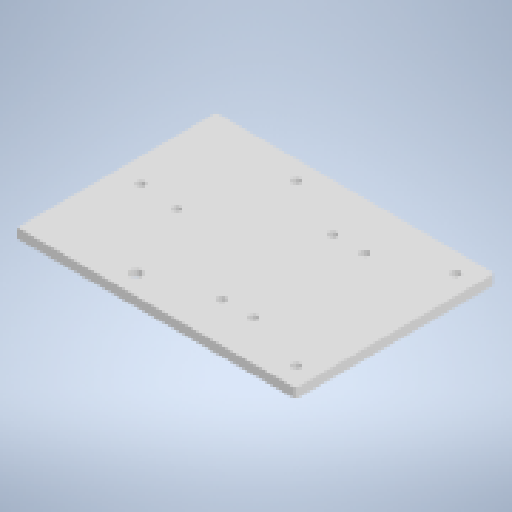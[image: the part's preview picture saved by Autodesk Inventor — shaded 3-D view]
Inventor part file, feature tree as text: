
AUTODESK INVENTOR PART (.ipt)
format: ipt  version: 2023.2 (Build 272271000, 271)  size: 173,056 bytes
history: native  units: mm
features: hole x4, reference x4, other x4, sketch x3, extrude x1, fillet x1
ambient origin geometry x8: Origin, YZ Plane, XZ Plane, XY Plane, X Axis, Y Axis, Z Axis, Center Point
bodies: Solid1 (feature_tree)
feature tree (17):
  sketch  "Sketch1"  dims[d0=125.2mm d1=125.2mm d2=12.3mm d3=12.3mm d8=50.0mm d9=6.0mm d10=0.0mm]
  extrude  "Extrusion1"  Depth=6.0mm
  fillet  "Fillet1"  Radius=6.0mm
  hole  "Hole1"  [1 undecoded]
  hole  "Hole2"  [1 undecoded]
  hole  "Hole3"  [1 undecoded]
  hole  "Hole4"  [1 undecoded]
  sketch  "Sketch2"  dims[d11=2.0mm d12=10.0mm]
  sketch  "Sketch3"  dims[d13=10.0mm d14=15.0mm d15=25.0mm d16=5.1mm d17=6.0mm d18=4.0mm d19=2.0mm d20=90.0deg d21=8.0mm d22=20.594885mm d27=5.1mm d28=6.0mm d29=4.0mm d30=2.0mm d31=90.0deg d32=8.0mm d33=20.594885mm d35=12.3mm d36=100.6mm d37=7.2mm d38=6.0mm d39=12.25mm d40=2.0mm d41=90.0deg d42=8.0mm d43=20.594885mm d44=5.1mm d45=6.0mm d46=9.2mm d47=2.0mm d48=90.0deg d49=8.0mm d50=20.594885mm]
  reference  "Reference1"
  reference  "Reference2"
  reference  "Reference3"
  reference  "Reference4"
  parser-record x1  (decoder bookkeeping rows leaked as tree rows — omitted from the tree; the rows remain in map.json)
  other  "Main Assembly.iam"
  other  "ACME-Nut-Block:1"
  other  "ACME-Nut-Block:2"
note: 4 required parameter values undecoded (feature->parameter linkage not recoverable at this tier; creation-order binding heuristic only, values carry confidence <= 0.55)
note: 1 file-system path scrubbed to <path> (originals preserved in map.json)
